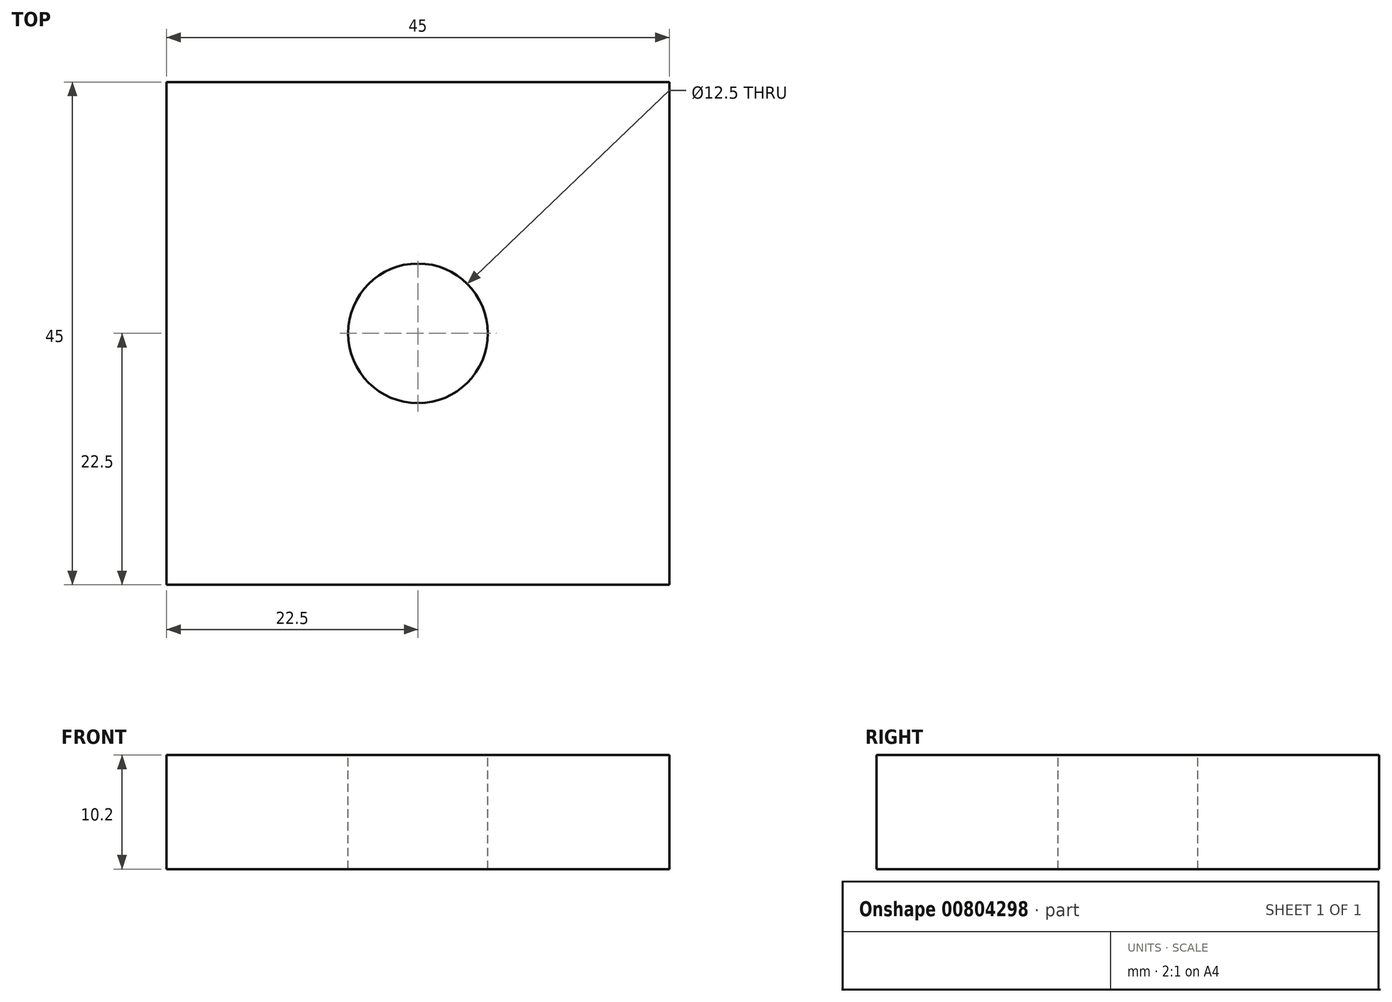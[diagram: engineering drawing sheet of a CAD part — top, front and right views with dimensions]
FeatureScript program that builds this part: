
annotation { "Feature Type Name" : "Feature", "Feature Type Description" : "" }
export const myFeature = defineFeature(function(context is Context, id is Id, definition is map)
    precondition{}
    {
        {
            var Q0;
            Q0=qCreatedBy(makeId("Top.planeOp"),FACE);
            var sketch = newSketch(context, id + "F0", { "sketchPlane" : qUnion([Q0])});
            skLineSegment(sketch, "E0.bottom", {"start": v(22.5, 22.5) * mm, "end": v(-22.5, 22.5) * mm});
            skLineSegment(sketch, "E0.top", {"start": v(22.5, -22.5) * mm, "end": v(-22.5, -22.5) * mm});
            skLineSegment(sketch, "E0.left", {"start": v(22.5, 22.5) * mm, "end": v(22.5, -22.5) * mm});
            skLineSegment(sketch, "E0.right", {"start": v(-22.5, 22.5) * mm, "end": v(-22.5, -22.5) * mm});
            skPoint(sketch, "E0.middle", {"position": v(0, 0) * mm});
            skSolve(sketch);
        }
        {
            var Q0;
            Q0=makeQuery(id+"F0.imprint","IMPRINT",FACE,{"disambiguationData":[TD([[makeQuery(id+"F0.imprint","IMPRINT",EDGE,{"derivedFrom":sQuery(id+"F0.wireOp",EDGE,"E0.bottom")}),1.0]])]});
            extrude(context, id + "F1", {"entities" : qUnion([Q0]), "depth" : 10.2 * mm, "offsetDistance" : 25.4 * mm});
        }
        {
            var Q0;
            Q0=makeQuery(id+"F1.opExtrude","CAP_FACE",FACE,{"disambiguationData":[OSD([sQuery(id+"F0.wireOp",EDGE,"E0.bottom"),sQuery(id+"F0.wireOp",EDGE,"E0.top"),sQuery(id+"F0.wireOp",EDGE,"E0.left"),sQuery(id+"F0.wireOp",EDGE,"E0.right")])],"isStart":false});
            var sketch = newSketch(context, id + "F2", { "sketchPlane" : qUnion([Q0])});
            skCircle(sketch, "E1", {"center": v(0, 0) * mm, "radius": 6.25 * mm});
            skSolve(sketch);
        }
        {
            var Q0;
            Q0 = qSketchRegion(id + "F2", true);
            extrude(context, id + "F3", {"entities" : qUnion([Q0]), "operationType" : NewBodyOperationType.REMOVE, "endBound" : BoundingType.THROUGH_ALL, "oppositeDirection" : true, "depth" : 2 * mm, "offsetDistance" : 25.4 * mm});
        }
    });
